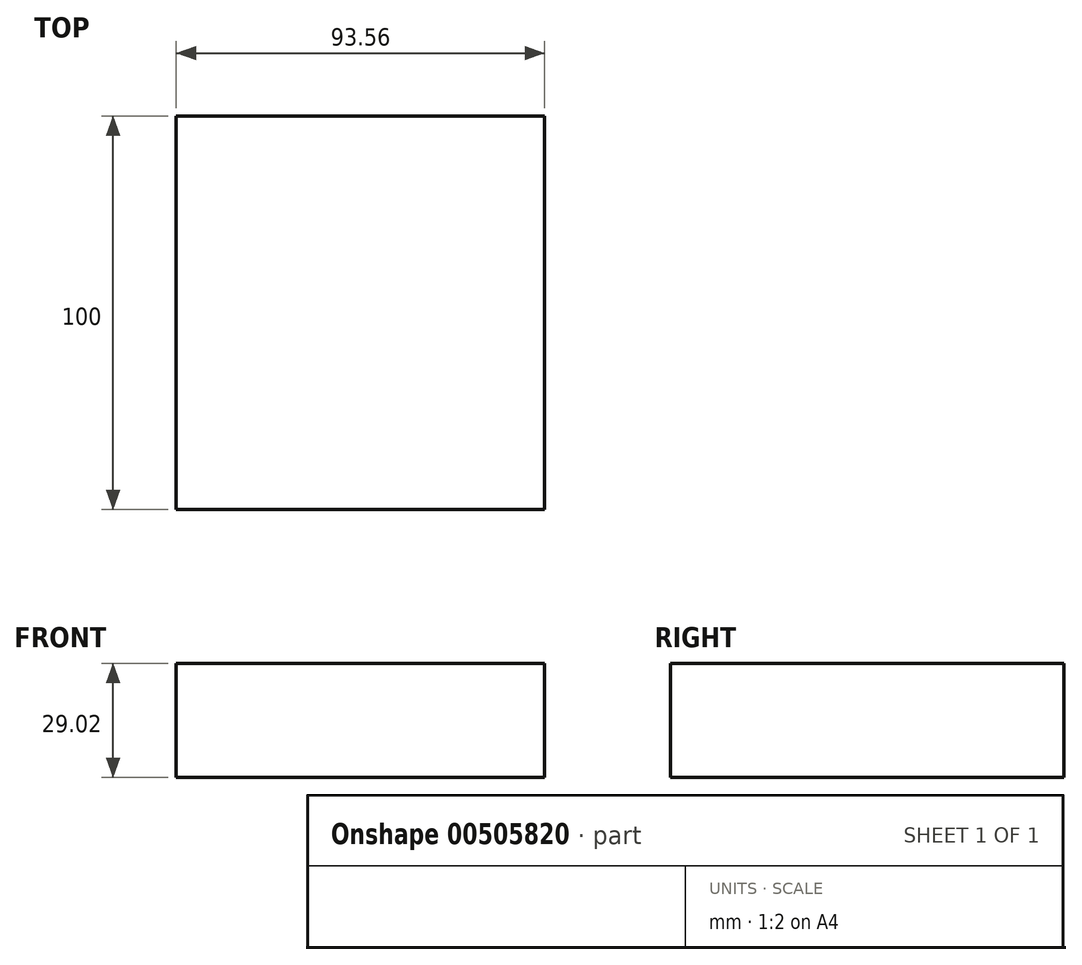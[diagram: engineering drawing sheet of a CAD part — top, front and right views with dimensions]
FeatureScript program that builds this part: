
annotation { "Feature Type Name" : "Feature", "Feature Type Description" : "" }
export const myFeature = defineFeature(function(context is Context, id is Id, definition is map)
    precondition{}
    {
        {
            var Q0;
            Q0=qCreatedBy(makeId("Front.planeOp"),FACE);
            var sketch = newSketch(context, id + "F0", { "sketchPlane" : qUnion([Q0])});
            skLineSegment(sketch, "E0.bottom", {"start": v(-46.78, 14.5) * mm, "end": v(46.78, 14.5) * mm});
            skLineSegment(sketch, "E0.top", {"start": v(-46.78, -14.5) * mm, "end": v(46.78, -14.5) * mm});
            skLineSegment(sketch, "E0.left", {"start": v(-46.78, 14.5) * mm, "end": v(-46.78, -14.5) * mm});
            skLineSegment(sketch, "E0.right", {"start": v(46.78, 14.5) * mm, "end": v(46.78, -14.5) * mm});
            skPoint(sketch, "E0.middle", {"position": v(0, 0) * mm});
            skSolve(sketch);
        }
        {
            var Q0;
            Q0 = qSketchRegion(id + "F0", true);
            extrude(context, id + "F1", {"entities" : qUnion([Q0]), "endBound" : BoundingType.SYMMETRIC, "depth" : 100 * mm});
        }
    });
